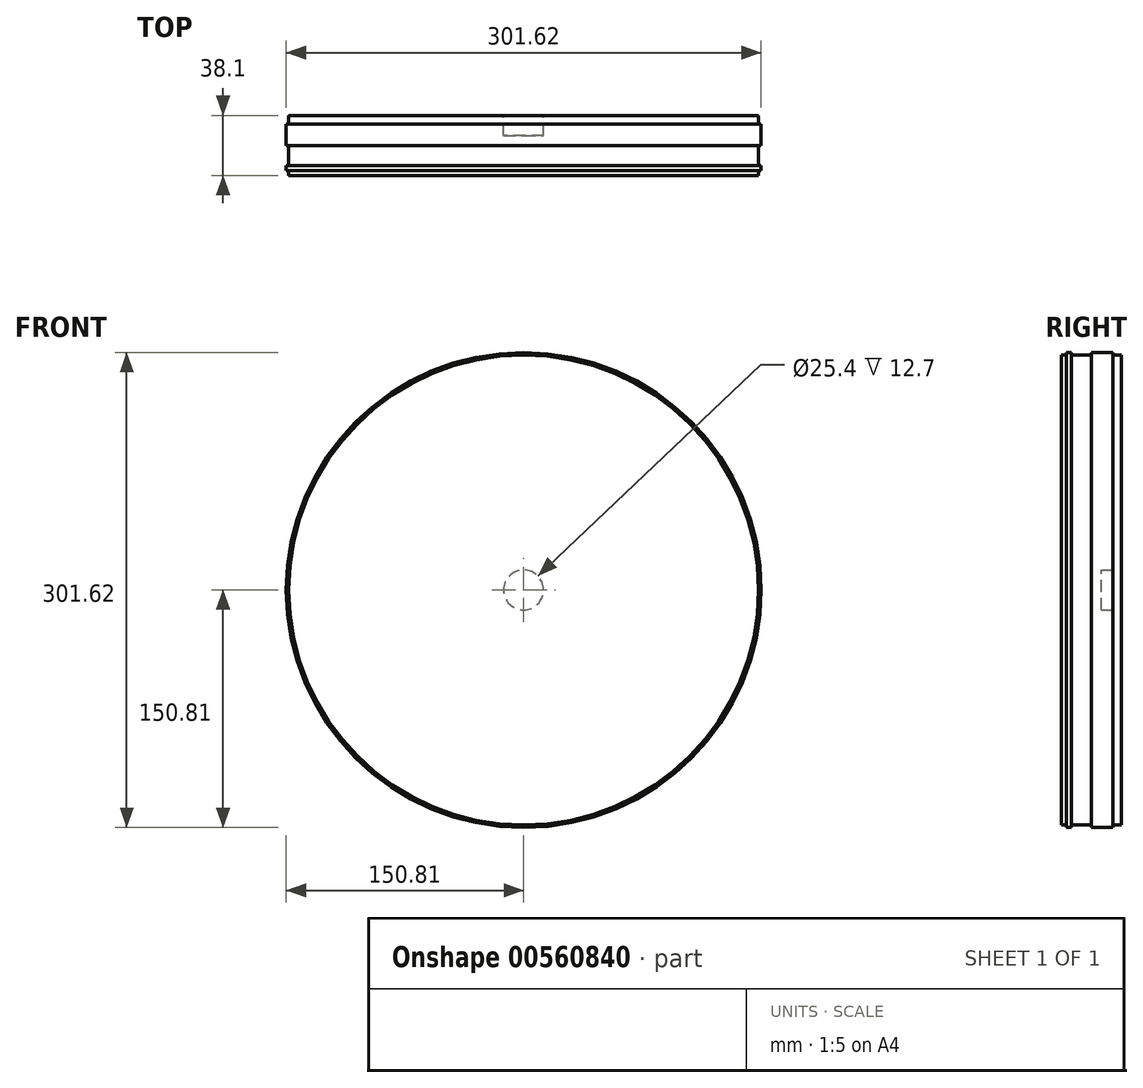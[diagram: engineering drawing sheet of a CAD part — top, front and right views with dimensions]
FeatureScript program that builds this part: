
annotation { "Feature Type Name" : "Feature", "Feature Type Description" : "" }
export const myFeature = defineFeature(function(context is Context, id is Id, definition is map)
    precondition{}
    {
        {
            var Q0;
            Q0=qCreatedBy(makeId("Front.planeOp"),FACE);
            var sketch = newSketch(context, id + "F0", { "sketchPlane" : qUnion([Q0])});
            skCircle(sketch, "E0", {"center": v(0, 0) * mm, "radius": 152.4 * mm});
            skSolve(sketch);
        }
        {
            var Q0;
            Q0 = qSketchRegion(id + "F0", true);
            extrude(context, id + "F1", {"entities" : qUnion([Q0]), "depth" : 38.1 * mm, "offsetDistance" : 25.4 * mm});
        }
        {
            var Q0;
            Q0=qCreatedBy(makeId("Right.planeOp"),FACE);
            var sketch = newSketch(context, id + "F2", { "sketchPlane" : qUnion([Q0])});
            skLineSegment(sketch, "E1", {"start": v(-38.1, 149.23) * mm, "end": v(-34.93, 149.23) * mm});
            skLineSegment(sketch, "E2", {"start": v(-34.93, 149.23) * mm, "end": v(-34.93, 150.81) * mm});
            skLineSegment(sketch, "E3", {"start": v(-34.93, 150.81) * mm, "end": v(-31.75, 150.81) * mm});
            skLineSegment(sketch, "E4", {"start": v(-31.75, 150.81) * mm, "end": v(-31.75, 149.23) * mm});
            skLineSegment(sketch, "E5", {"start": v(-31.75, 149.23) * mm, "end": v(-19.05, 149.23) * mm});
            skLineSegment(sketch, "E6", {"start": v(-19.05, 149.23) * mm, "end": v(-19.05, 150.81) * mm});
            skLineSegment(sketch, "E7", {"start": v(-19.05, 150.81) * mm, "end": v(-5.6, 150.81) * mm});
            skLineSegment(sketch, "E8", {"start": v(-5.6, 150.81) * mm, "end": v(-5.6, 149.23) * mm});
            skLineSegment(sketch, "E9", {"start": v(-5.6, 149.23) * mm, "end": v(0, 149.23) * mm});
            skLineSegment(sketch, "E10", {"start": v(0, 149.23) * mm, "end": v(0, 152.9) * mm});
            skLineSegment(sketch, "E11", {"start": v(0, 152.9) * mm, "end": v(-38.1, 152.9) * mm});
            skLineSegment(sketch, "E12", {"start": v(-38.1, 152.9) * mm, "end": v(-38.1, 149.23) * mm});
            skLineSegment(sketch, "E13", {"start": v(0, 0) * mm, "end": v(-53.27, 0) * mm, "construction": true});
            skSolve(sketch);
        }
        {
            var Q0;
            Q0 = qSketchRegion(id + "F2", true);
            var Q1;
            Q1=sQuery(id+"F2.wireOp",EDGE,"E13");
            revolve(context, id + "F3", {"operationType" : NewBodyOperationType.REMOVE, "entities" : qUnion([Q0]), "axis" : qUnion([Q1]), "revolveType" : RevolveType.FULL, "oppositeDirection" : true});
        }
        {
            var Q0;
            Q0=makeQuery(id+"F0.imprint","IMPRINT",FACE,{"disambiguationData":[TD([[makeQuery(id+"F0.imprint","IMPRINT",EDGE,{"derivedFrom":sQuery(id+"F0.wireOp",EDGE,"E0")}),1.0]])]});
            var sketch = newSketch(context, id + "F4", { "sketchPlane" : qUnion([Q0])});
            skCircle(sketch, "E14", {"center": v(0, 0) * mm, "radius": 12.7 * mm});
            skSolve(sketch);
        }
        {
            var Q0;
            Q0 = qSketchRegion(id + "F4", true);
            extrude(context, id + "F5", {"entities" : qUnion([Q0]), "operationType" : NewBodyOperationType.REMOVE, "depth" : 12.7 * mm, "offsetDistance" : 25.4 * mm});
        }
    });
